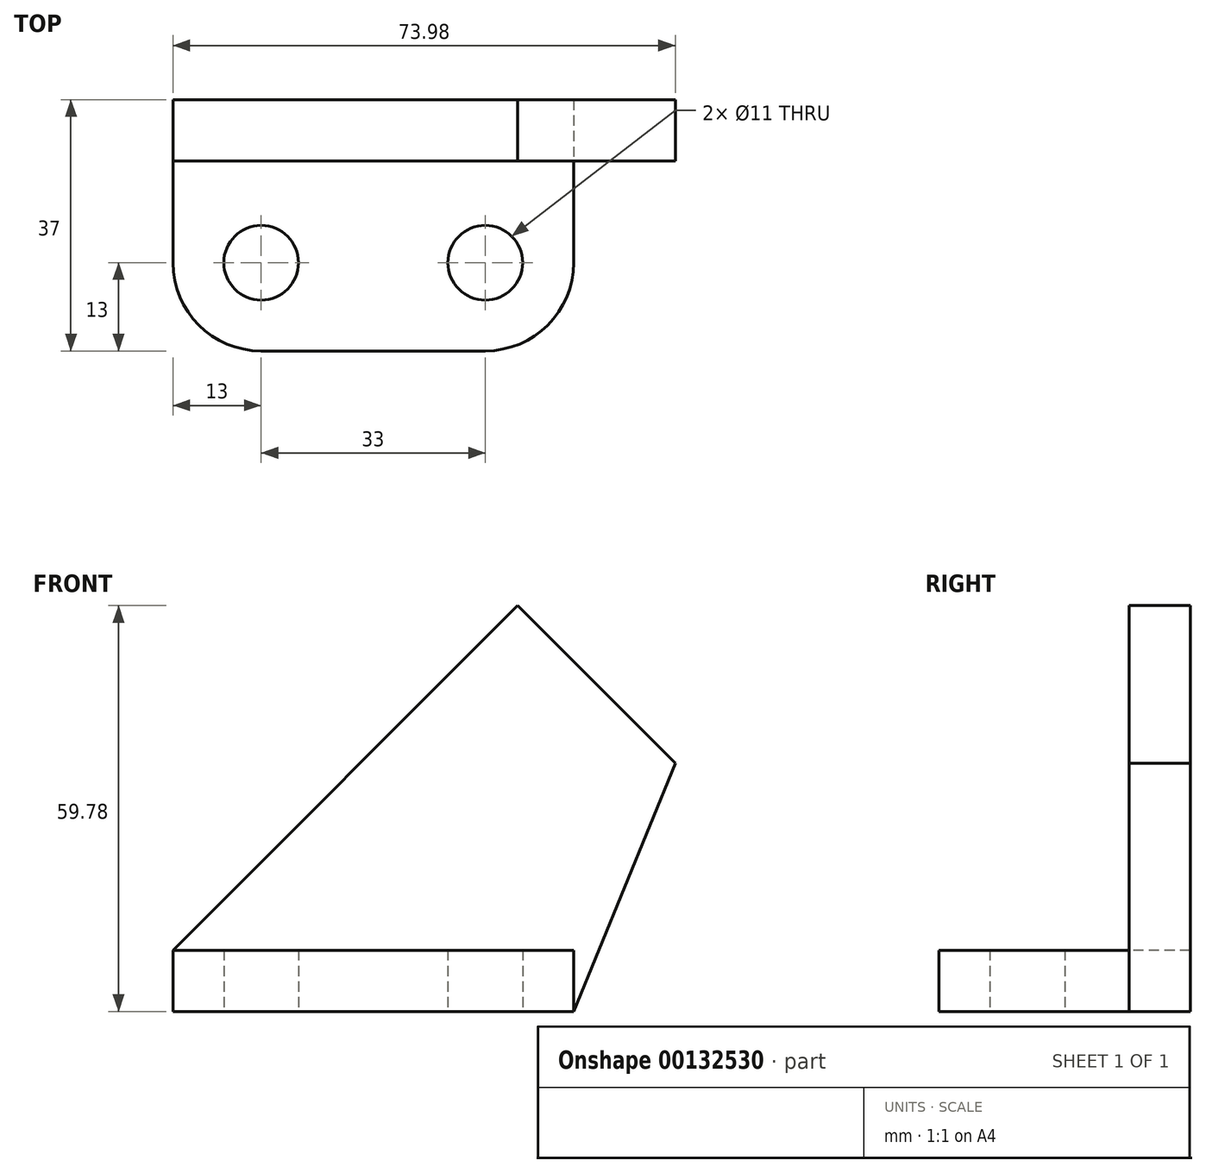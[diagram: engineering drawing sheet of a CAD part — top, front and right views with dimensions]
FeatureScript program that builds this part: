
annotation { "Feature Type Name" : "Feature", "Feature Type Description" : "" }
export const myFeature = defineFeature(function(context is Context, id is Id, definition is map)
    precondition{}
    {
        {
            var Q0;
            Q0=qCreatedBy(makeId("Top.planeOp"),FACE);
            var sketch = newSketch(context, id + "F0", { "sketchPlane" : qUnion([Q0])});
            skLineSegment(sketch, "E0", {"start": v(0, 37) * mm, "end": v(0, 13) * mm});
            skLineSegment(sketch, "E1", {"start": v(13, 0) * mm, "end": v(46, 0) * mm});
            skLineSegment(sketch, "E2", {"start": v(59, 37) * mm, "end": v(59, 13) * mm});
            skArc(sketch, "E3", {"start": v(46, 0) * mm, "mid": v(55.2, 3.8) * mm, "end": v(59, 13) * mm});
            skArc(sketch, "E4", {"start": v(0, 13) * mm, "mid": v(3.8, 3.8) * mm, "end": v(13, 0) * mm});
            skLineSegment(sketch, "E5", {"start": v(0, 37) * mm, "end": v(59, 37) * mm});
            skCircle(sketch, "E6", {"center": v(13, 13) * mm, "radius": 5.5 * mm});
            skCircle(sketch, "E7", {"center": v(46, 13) * mm, "radius": 5.5 * mm});
            skLineSegment(sketch, "E8", {"start": v(13, 13) * mm, "end": v(173.35, 13) * mm, "construction": true});
            skSolve(sketch);
        }
        {
            var Q0;
            Q0=makeQuery(id+"F0.imprint","IMPRINT",FACE,{"disambiguationData":[TD([[makeQuery(id+"F0.imprint","IMPRINT",EDGE,{"derivedFrom":sQuery(id+"F0.wireOp",EDGE,"E0")}),1.0]])]});
            extrude(context, id + "F1", {"entities" : qUnion([Q0]), "depth" : (9) * mm});
        }
        {
            var Q0;
            Q0=makeQuery(id+"F1.opExtrude","SWEPT_FACE",FACE,{"disambiguationData":[OSD([sQuery(id+"F0.wireOp",EDGE,"E5")])]});
            var sketch = newSketch(context, id + "F2", { "sketchPlane" : qUnion([Q0])});
            skLineSegment(sketch, "E9.0", {"start": v(0, 9) * mm, "end": v(-59, 9) * mm});
            skLineSegment(sketch, "E10", {"start": v(0, 9) * mm, "end": v(-50.78, 59.78) * mm});
            skLineSegment(sketch, "E11", {"start": v(-59, 0) * mm, "end": v(-73.98, 36.57) * mm});
            skLineSegment(sketch, "E12", {"start": v(-50.78, 59.78) * mm, "end": v(-73.98, 36.57) * mm});
            skLineSegment(sketch, "E13", {"start": v(-50.78, 59.78) * mm, "end": v(-115.97, 59.78) * mm, "construction": true});
            skSolve(sketch);
        }
        {
            var Q0;
            Q0=makeQuery(id+"F2.imprint","IMPRINT",FACE,{"disambiguationData":[TD([[makeQuery(id+"F2.imprint","IMPRINT",EDGE,{"derivedFrom":sQuery(id+"F2.wireOp",EDGE,"E9.0")}),-1.0]])]});
            extrude(context, id + "F3", {"entities" : qUnion([Q0]), "operationType" : NewBodyOperationType.ADD, "oppositeDirection" : true, "depth" : (9) * mm});
        }
    });
